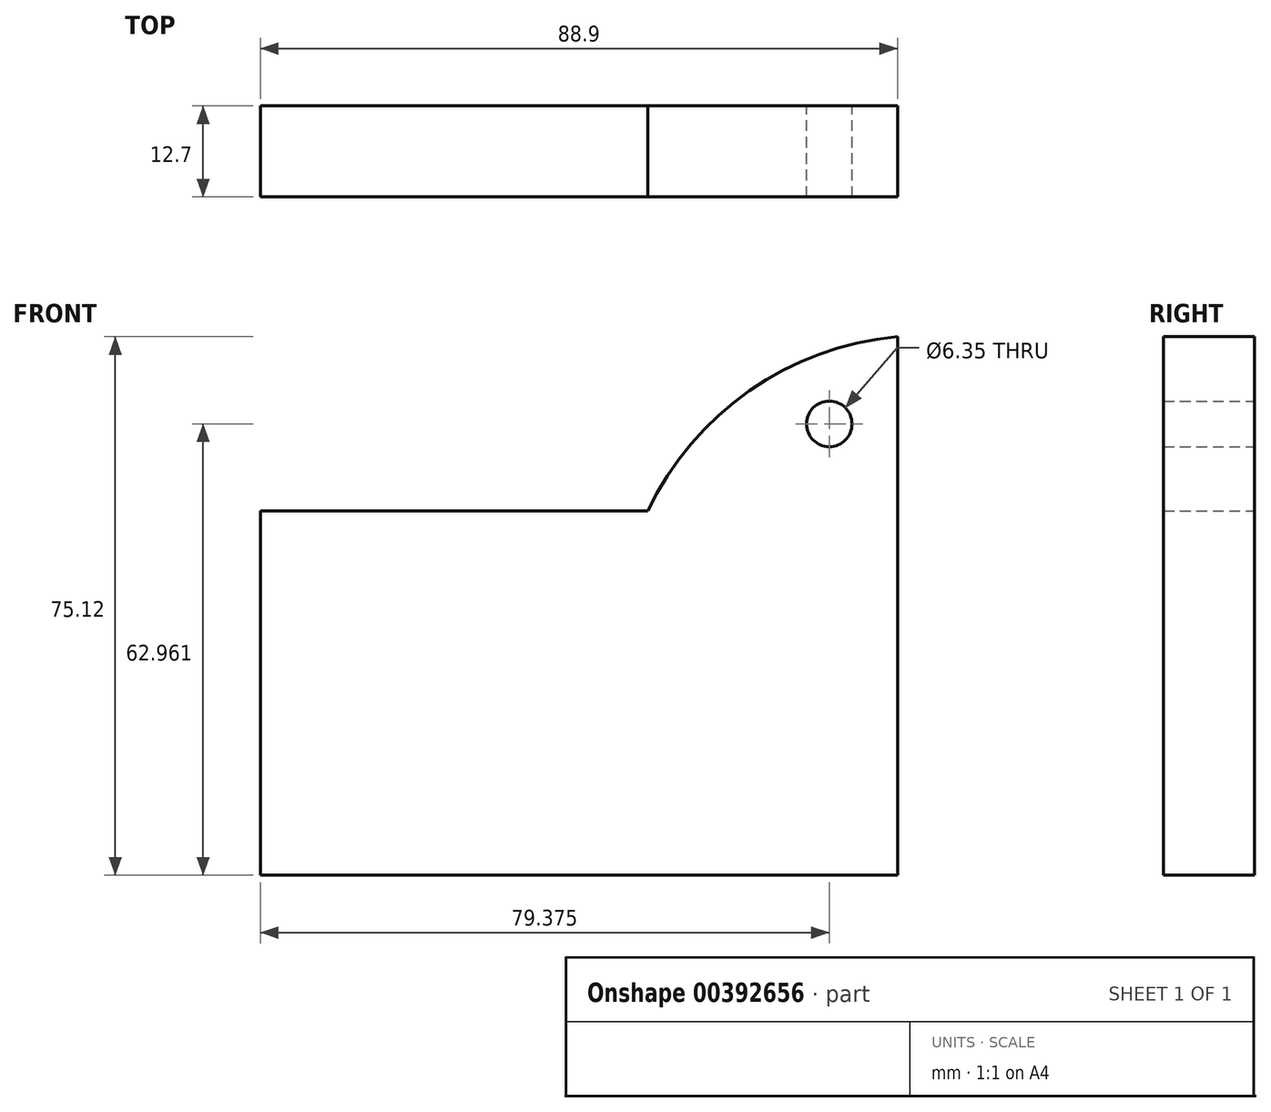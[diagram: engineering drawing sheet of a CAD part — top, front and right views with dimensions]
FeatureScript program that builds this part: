
annotation { "Feature Type Name" : "Feature", "Feature Type Description" : "" }
export const myFeature = defineFeature(function(context is Context, id is Id, definition is map)
    precondition{}
    {
        {
            var Q0;
            Q0=qCreatedBy(makeId("Front.planeOp"),FACE);
            var sketch = newSketch(context, id + "F0", { "sketchPlane" : qUnion([Q0])});
            skLineSegment(sketch, "E0.bottom", {"start": v(-44.45, -25.4) * mm, "end": v(44.45, -25.4) * mm});
            skLineSegment(sketch, "E0.top", {"start": v(-44.45, 25.4) * mm, "end": v(44.45, 25.4) * mm});
            skLineSegment(sketch, "E0.left", {"start": v(-44.45, -25.4) * mm, "end": v(-44.45, 25.4) * mm});
            skLineSegment(sketch, "E0.right", {"start": v(44.45, -25.4) * mm, "end": v(44.45, 25.4) * mm});
            skPoint(sketch, "E0.middle", {"position": v(0, 0) * mm});
            skLineSegment(sketch, "E1", {"start": v(44.45, 25.4) * mm, "end": v(44.45, 49.72) * mm});
            skArc(sketch, "E2", {"start": v(44.45, 49.72) * mm, "mid": v(23.8, 42.18) * mm, "end": v(9.6, 25.4) * mm});
            skSolve(sketch);
        }
        {
            var Q0;
            Q0 = qSketchRegion(id + "F0", true);
            extrude(context, id + "F1", {"entities" : qUnion([Q0]), "depth" : 12.7 * mm});
        }
        {
            var Q0;
            Q0=qCreatedBy(makeId("Front.planeOp"),FACE);
            var sketch = newSketch(context, id + "F2", { "sketchPlane" : qUnion([Q0])});
            skPoint(sketch, "E3", {"position": v(34.93, 37.56) * mm});
            skSolve(sketch);
        }
        {
            var Q0;
            Q0=sQuery(id+"F2.wireOp",VERTEX,"E3");
            var Q1;
            Q1=makeQuery(id+"F1.opExtrude","SWEPT_BODY",BODY,{"disambiguationData":[OSD([sQuery(id+"F0.wireOp",EDGE,"E0.bottom"),sQuery(id+"F0.wireOp",EDGE,"E0.top"),sQuery(id+"F0.wireOp",EDGE,"E0.left"),sQuery(id+"F0.wireOp",EDGE,"E0.right"),sQuery(id+"F0.wireOp",EDGE,"E1"),sQuery(id+"F0.wireOp",EDGE,"E2")])]});
            hole(context, id + "F3", {"style" : HoleStyle.SIMPLE, "endStyle" : HoleEndStyle.THROUGH, "oppositeDirection" : true, "holeDiameter" : 6.35 * mm, "isTappedThrough" : true, "tappedDepth" : 12.7 * mm, "tapClearance" : 3, "locations" : qUnion([Q0]), "scope" : qUnion([Q1])});
        }
    });
